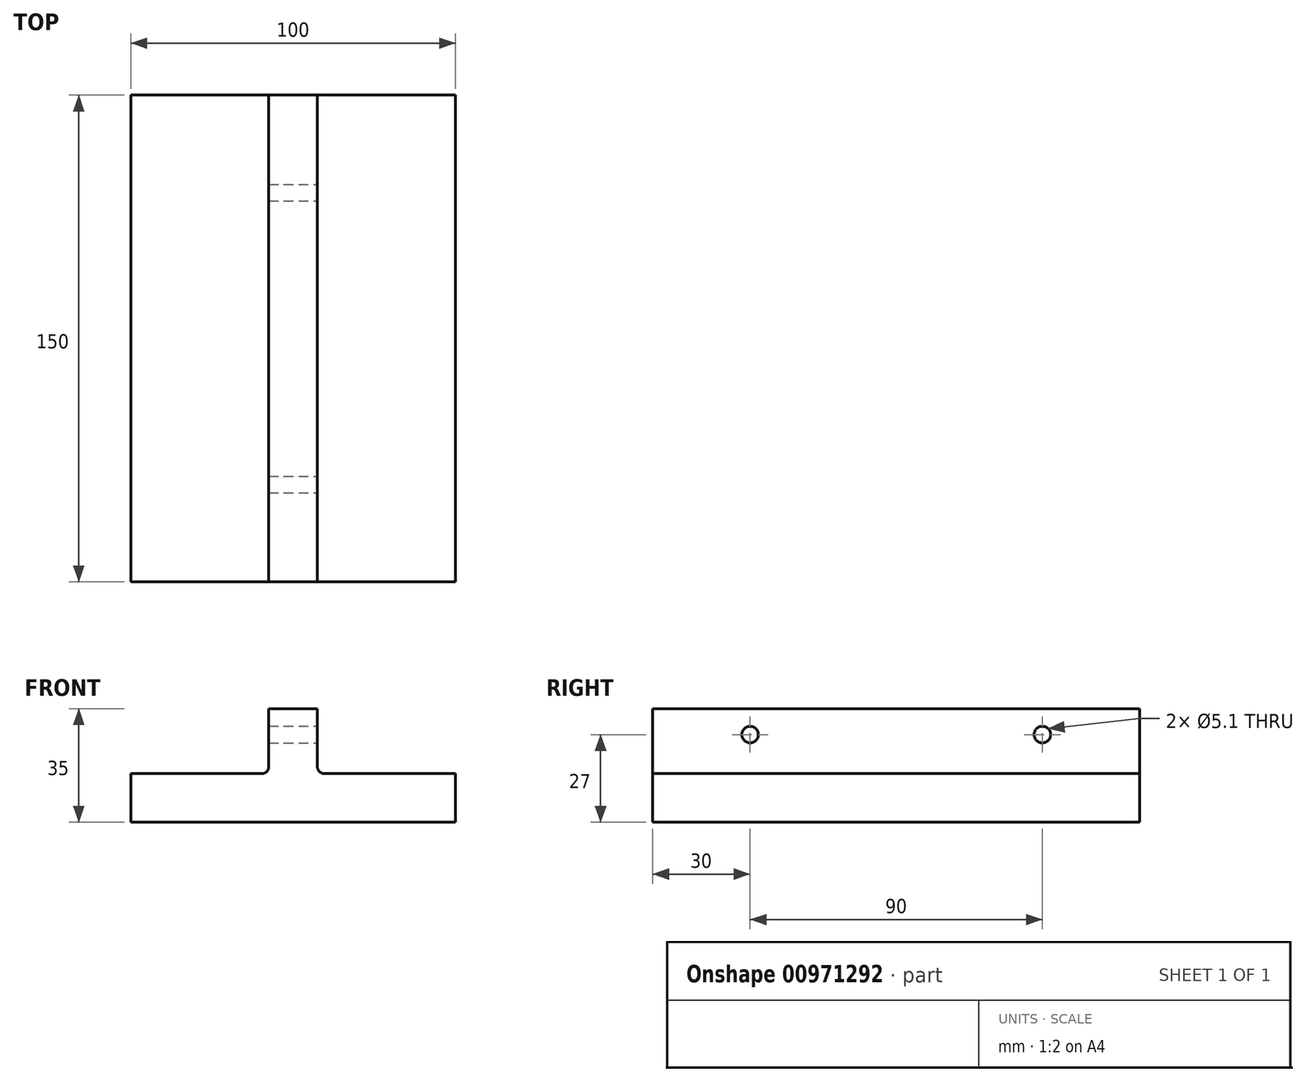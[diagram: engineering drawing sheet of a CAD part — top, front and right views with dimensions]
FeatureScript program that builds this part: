
annotation { "Feature Type Name" : "Feature", "Feature Type Description" : "" }
export const myFeature = defineFeature(function(context is Context, id is Id, definition is map)
    precondition{}
    {
        {
            var Q0;
            Q0=qCreatedBy(makeId("Front.planeOp"),FACE);
            var sketch = newSketch(context, id + "F0", { "sketchPlane" : qUnion([Q0])});
            skLineSegment(sketch, "E0", {"start": v(-53.17, 0) * mm, "end": v(46.83, 0) * mm});
            skLineSegment(sketch, "E1", {"start": v(46.83, 0) * mm, "end": v(46.83, 15) * mm});
            skLineSegment(sketch, "E2", {"start": v(46.83, 15) * mm, "end": v(4.33, 15) * mm});
            skLineSegment(sketch, "E3", {"start": v(4.33, 15) * mm, "end": v(4.33, 35) * mm});
            skLineSegment(sketch, "E4", {"start": v(4.33, 35) * mm, "end": v(-10.67, 35) * mm});
            skLineSegment(sketch, "E5", {"start": v(-10.67, 35) * mm, "end": v(-10.67, 15) * mm});
            skLineSegment(sketch, "E6", {"start": v(-10.67, 15) * mm, "end": v(-53.17, 15) * mm});
            skLineSegment(sketch, "E7", {"start": v(-53.17, 15) * mm, "end": v(-53.17, 0) * mm});
            skSolve(sketch);
        }
        {
            var Q0;
            Q0=makeQuery(id+"F0.imprint","IMPRINT",FACE,{"disambiguationData":[TD([[makeQuery(id+"F0.imprint","IMPRINT",EDGE,{"derivedFrom":sQuery(id+"F0.wireOp",EDGE,"E0")}),1.0]])]});
            extrude(context, id + "F1", {"entities" : qUnion([Q0]), "depth" : 150 * mm, "offsetDistance" : 25 * mm});
        }
        {
            var Q0;
            Q0=makeQuery(id+"F1.opExtrude","SWEPT_FACE",FACE,{"disambiguationData":[OSD([sQuery(id+"F0.wireOp",EDGE,"E3")])]});
            var sketch = newSketch(context, id + "F2", { "sketchPlane" : qUnion([Q0])});
            skCircle(sketch, "E8", {"center": v(-120, 27) * mm, "radius": 2.55 * mm});
            skCircle(sketch, "E9", {"center": v(-30, 27) * mm, "radius": 2.55 * mm});
            skSolve(sketch);
        }
        {
            var Q0;
            Q0=makeQuery(id+"F2.imprint","IMPRINT",FACE,{"disambiguationData":[TD([[makeQuery(id+"F2.imprint","IMPRINT",EDGE,{"derivedFrom":sQuery(id+"F2.wireOp",EDGE,"E8")}),1.0]])]});
            var Q1;
            Q1=makeQuery(id+"F2.imprint","IMPRINT",FACE,{"disambiguationData":[TD([[makeQuery(id+"F2.imprint","IMPRINT",EDGE,{"derivedFrom":sQuery(id+"F2.wireOp",EDGE,"E9")}),1.0]])]});
            var Q2;
            Q2=sQuery(id+"F2.wireOp",EDGE,"E8");
            var Q3;
            Q3=sQuery(id+"F2.wireOp",EDGE,"E9");
            var Q4;
            Q4=makeQuery(id+"F1.opExtrude","SWEPT_FACE",FACE,{"disambiguationData":[OSD([sQuery(id+"F0.wireOp",EDGE,"E5")])]});
            extrude(context, id + "F3", {"entities" : qUnion([Q0, Q1]), "operationType" : NewBodyOperationType.REMOVE, "surfaceEntities" : qUnion([Q2, Q3]), "endBound" : BoundingType.UP_TO_SURFACE, "oppositeDirection" : true, "depth" : 25 * mm, "endBoundEntityFace" : qUnion([Q4]), "offsetDistance" : 25 * mm});
        }
        {
            var Q0;
            Q0=makeQuery(id+"F1.opExtrude","SWEPT_EDGE",EDGE,{"disambiguationData":[OSD([sQuery(id+"F0.wireOp",EDGE,"E5"),sQuery(id+"F0.wireOp",EDGE,"E6")])]});
            var Q1;
            Q1=makeQuery(id+"F1.opExtrude","SWEPT_EDGE",EDGE,{"disambiguationData":[OSD([sQuery(id+"F0.wireOp",EDGE,"E2"),sQuery(id+"F0.wireOp",EDGE,"E3")])]});
            fillet(context, id + "F4", {"entities" : qUnion([Q0, Q1]), "radius" : 2 * mm, "tangentPropagation" : true, "allowEdgeOverflow" : false});
        }
    });
